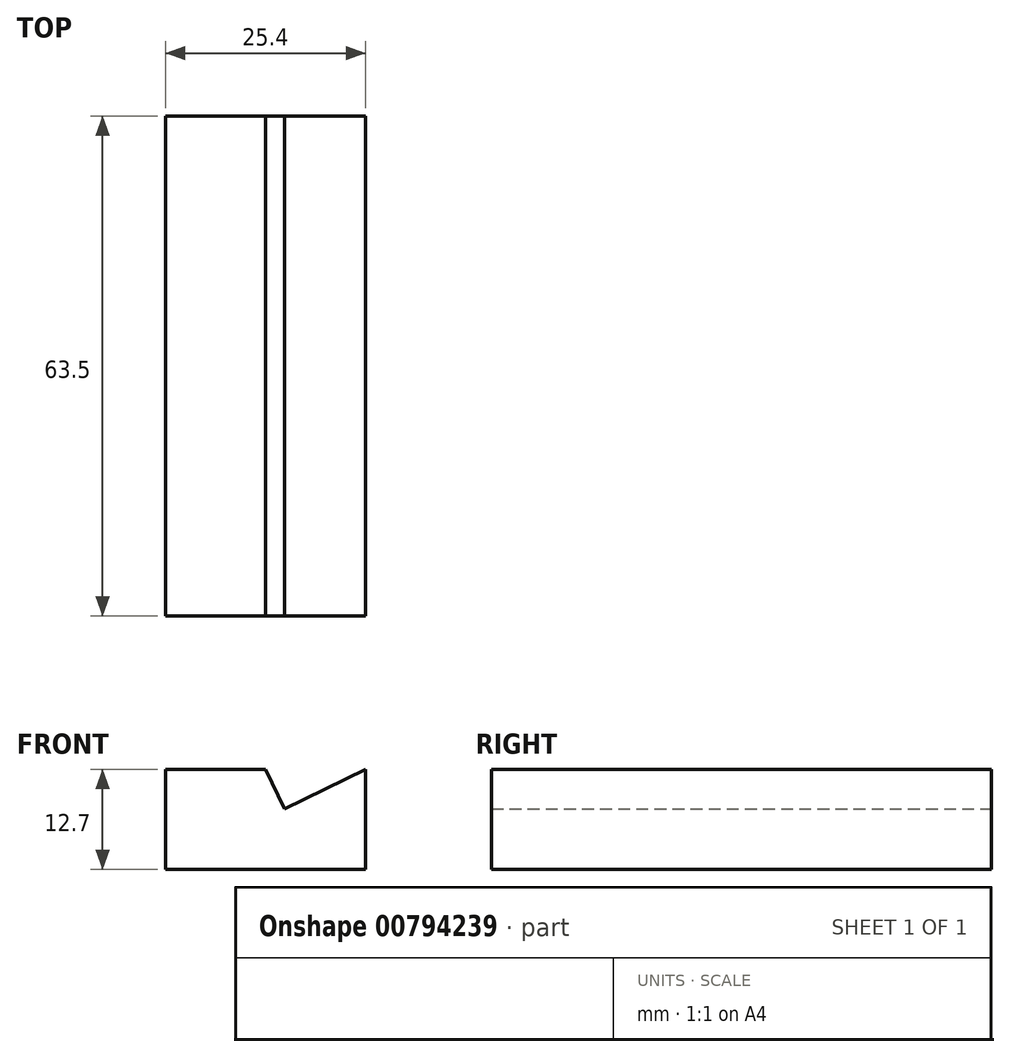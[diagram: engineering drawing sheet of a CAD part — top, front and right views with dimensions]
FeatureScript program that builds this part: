
annotation { "Feature Type Name" : "Feature", "Feature Type Description" : "" }
export const myFeature = defineFeature(function(context is Context, id is Id, definition is map)
    precondition{}
    {
        {
            var Q0;
            Q0=qCreatedBy(makeId("Front.planeOp"),FACE);
            var sketch = newSketch(context, id + "F0", { "sketchPlane" : qUnion([Q0])});
            skLineSegment(sketch, "E0", {"start": v(-28.28, 23) * mm, "end": v(-28.28, 10.3) * mm});
            skLineSegment(sketch, "E1", {"start": v(-28.28, 10.3) * mm, "end": v(-2.88, 10.3) * mm});
            skLineSegment(sketch, "E2", {"start": v(-2.88, 10.3) * mm, "end": v(-2.88, 23) * mm});
            skLineSegment(sketch, "E3", {"start": v(-2.88, 23) * mm, "end": v(-13.17, 18.02) * mm});
            skLineSegment(sketch, "E4", {"start": v(-13.17, 18.02) * mm, "end": v(-15.58, 23) * mm});
            skLineSegment(sketch, "E5", {"start": v(-15.58, 23) * mm, "end": v(-28.28, 23) * mm});
            skSolve(sketch);
        }
        {
            var Q0;
            Q0=makeQuery(id+"F0.imprint","IMPRINT",FACE,{"disambiguationData":[TD([[makeQuery(id+"F0.imprint","IMPRINT",EDGE,{"derivedFrom":sQuery(id+"F0.wireOp",EDGE,"E0")}),1.0]])]});
            extrude(context, id + "F1", {"entities" : qUnion([Q0]), "depth" : 63.5 * mm, "offsetDistance" : 25.4 * mm});
        }
    });
